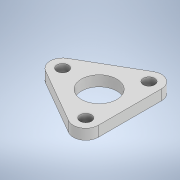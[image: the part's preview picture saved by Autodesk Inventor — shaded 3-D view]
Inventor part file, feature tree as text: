
AUTODESK INVENTOR PART (.ipt)
format: ipt  version: 2021 (Build 250183000, 183)  size: 125,952 bytes
history: native  units: mm
features: extrude x1, sketch x1
ambient origin geometry x8: Origin, YZ Plane, XZ Plane, XY Plane, X Axis, Y Axis, Z Axis, Center Point
bodies: Solid1 (feature_tree)
feature tree (2):
  extrude  "Extrusion1"  TaperAngle=120.0deg  [1 undecoded]
  sketch  "Sketch1"  dims[d0=120.0deg d1=120.0deg d2=120.0deg d3=35.0mm d5=34.0mm d6=35.0mm d7=35.0mm d8=24.0mm d9=24.0mm d10=24.0mm d11=11.0mm d13=11.0mm d14=11.0mm d15=10.0mm d16=0.0mm]
note: 1 required parameter value undecoded (feature->parameter linkage not recoverable at this tier; creation-order binding heuristic only, values carry confidence <= 0.55)
